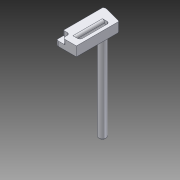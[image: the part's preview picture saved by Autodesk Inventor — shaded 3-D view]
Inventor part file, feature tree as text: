
AUTODESK INVENTOR PART (.ipt)
format: ipt  version: 2012 (Build 160160000, 160)  size: 131,072 bytes
history: native  units: mm
features: fillet x5, extrude x4, sketch x2, chamfer x1
ambient origin geometry x8: Origin, YZ Plane, XZ Plane, XY Plane, X Axis, Y Axis, Z Axis, Center Point
bodies: Solid1 (feature_tree)
feature tree (12):
  sketch  "Sketch1"  dims[d0=6.0mm d1=37.0mm]
  extrude  "Extrusion1"  Depth=37.0mm
  extrude  "Extrusion2"  TaperAngle=75.0deg  [1 undecoded]
  chamfer  "Chamfer1"  Distance=8.0mm
  extrude  "Extrusion3"  Depth=85.0mm TaperAngle=0.0deg
  fillet  "Fillet1"  Radius=3.0mm
  fillet  "Fillet2"  Radius=1.0mm
  fillet  "Fillet3"  Radius=6.4mm
  fillet  "Fillet4"  Radius=6.0mm
  fillet  "Fillet5"  Radius=4.0mm
  extrude  "Extrusion4"  Depth=2.0mm
  sketch  "Sketch2"  dims[d2=18.0mm d3=75.0deg d4=8.0mm d5=0.0mm d6=85.0mm d7=0.0mm d8=3.0mm d9=1.0mm d10=2.0mm d11=45.0deg d12=6.4mm d13=6.0mm d14=4.0mm d15=0.0mm d16=2.0mm d17=1.0mm d18=4.0mm d19=3.0mm d20=6.0mm d21=6.0mm d22=2.0mm d23=2.0mm d24=2.0mm d25=0.0mm d26=0.0mm]
note: 1 required parameter value undecoded (feature->parameter linkage not recoverable at this tier; creation-order binding heuristic only, values carry confidence <= 0.55)
